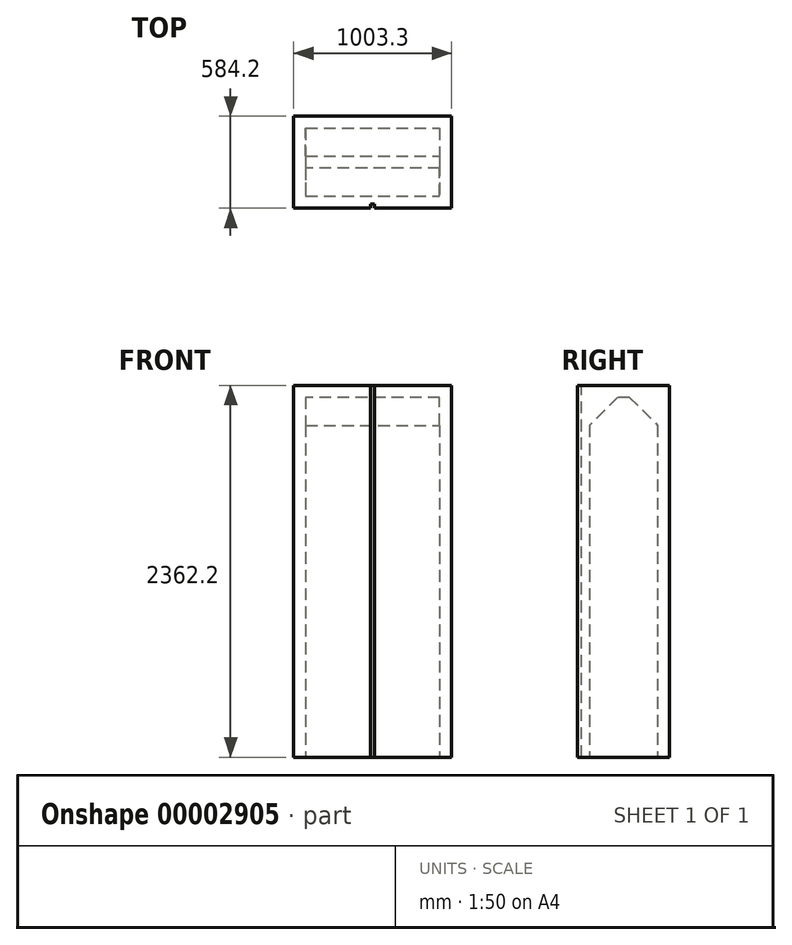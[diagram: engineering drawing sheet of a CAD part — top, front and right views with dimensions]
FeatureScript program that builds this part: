
annotation { "Feature Type Name" : "Feature", "Feature Type Description" : "" }
export const myFeature = defineFeature(function(context is Context, id is Id, definition is map)
    precondition{}
    {
        {
            var Q0;
            Q0=qCreatedBy(makeId("Top.planeOp"),FACE);
            var sketch = newSketch(context, id + "F0", { "sketchPlane" : qUnion([Q0])});
            skLineSegment(sketch, "E0.bottom", {"start": v(-500, 215.46) * mm, "end": v(503.3, 215.46) * mm});
            skLineSegment(sketch, "E0.top", {"start": v(-500, -368.74) * mm, "end": v(503.3, -368.74) * mm});
            skLineSegment(sketch, "E0.left", {"start": v(-500, 215.46) * mm, "end": v(-500, -368.74) * mm});
            skLineSegment(sketch, "E0.right", {"start": v(503.3, 215.46) * mm, "end": v(503.3, -368.74) * mm});
            skSolve(sketch);
        }
        {
            var Q0;
            Q0 = qSketchRegion(id + "F0", true);
            extrude(context, id + "F1", {"entities" : qUnion([Q0]), "depth" : 2362.2 * mm});
        }
        {
            var Q0;
            Q0=makeQuery(id+"F1.opExtrude","SWEPT_FACE",FACE,{"disambiguationData":[OSD([sQuery(id+"F0.wireOp",EDGE,"E0.top")])]});
            var sketch = newSketch(context, id + "F2", { "sketchPlane" : qUnion([Q0])});
            skLineSegment(sketch, "E1.bottom", {"start": v(12.7, 0) * mm, "end": v(-12.7, 0) * mm});
            skLineSegment(sketch, "E1.top", {"start": v(12.7, 2362.2) * mm, "end": v(-12.7, 2362.2) * mm});
            skLineSegment(sketch, "E1.left", {"start": v(12.7, 0) * mm, "end": v(12.7, 2362.2) * mm});
            skLineSegment(sketch, "E1.right", {"start": v(-12.7, 0) * mm, "end": v(-12.7, 2362.2) * mm});
            skSolve(sketch);
        }
        {
            var Q0;
            Q0 = qSketchRegion(id + "F2", true);
            extrude(context, id + "F3", {"entities" : qUnion([Q0]), "operationType" : NewBodyOperationType.REMOVE, "oppositeDirection" : true, "depth" : 25.4 * mm});
        }
        {
            var Q0;
            Q0=makeQuery(id+"F1.opExtrude","CAP_FACE",FACE,{"disambiguationData":[OSD([sQuery(id+"F0.wireOp",EDGE,"E0.bottom"),sQuery(id+"F0.wireOp",EDGE,"E0.top"),sQuery(id+"F0.wireOp",EDGE,"E0.left"),sQuery(id+"F0.wireOp",EDGE,"E0.right")])],"isStart":true});
            shell(context, id + "F4", {"entities" : qUnion([Q0]), "thickness" : 76.2 * mm});
        }
        {
            var Q0;
            Q0=makeQuery(id+"F1.opExtrude","CAP_FACE",FACE,{"disambiguationData":[OSD([sQuery(id+"F0.wireOp",EDGE,"E0.bottom"),sQuery(id+"F0.wireOp",EDGE,"E0.top"),sQuery(id+"F0.wireOp",EDGE,"E0.left"),sQuery(id+"F0.wireOp",EDGE,"E0.right")])],"isStart":true});
            var sketch = newSketch(context, id + "F5", { "sketchPlane" : qUnion([Q0])});
            skLineSegment(sketch, "E2.bottom", {"start": v(-88.9, 267.14) * mm, "end": v(88.9, 267.14) * mm});
            skLineSegment(sketch, "E2.top", {"start": v(-88.9, 292.54) * mm, "end": v(88.9, 292.54) * mm});
            skLineSegment(sketch, "E2.left", {"start": v(-88.9, 267.14) * mm, "end": v(-88.9, 292.54) * mm});
            skLineSegment(sketch, "E2.right", {"start": v(88.9, 267.14) * mm, "end": v(88.9, 292.54) * mm});
            skSolve(sketch);
        }
        {
            var Q0;
            Q0 = qSketchRegion(id + "F5", true);
            var Q1;
            Q1=makeQuery(id+"F4.opShell","OFFSET_FACE",FACE,{"disambiguationData":[OSD([sQuery(id+"F0.wireOp",EDGE,"E0.bottom"),sQuery(id+"F0.wireOp",EDGE,"E0.top"),sQuery(id+"F0.wireOp",EDGE,"E0.left"),sQuery(id+"F0.wireOp",EDGE,"E0.right")])]});
            extrude(context, id + "F6", {"entities" : qUnion([Q0]), "operationType" : NewBodyOperationType.REMOVE, "endBound" : BoundingType.UP_TO_SURFACE, "oppositeDirection" : true, "endBoundEntityFace" : qUnion([Q1]), "depth" : 25.4 * mm});
        }
        {
            var Q0;
            {var subQ0=sQuery(id+"F0.wireOp",EDGE,"E0.top");var subQ1=makeQuery(id+"F1.opExtrude","CAP_EDGE",EDGE,{"disambiguationData":[OSD([subQ0])],"isStart":false});var subQ2=sQuery(id+"F0.wireOp",EDGE,"E0.left");var subQ4=sQuery(id+"F0.wireOp",EDGE,"E0.right");Q0=makeQuery(id+"F6.boolean.opBoolean","MERGE",EDGE,{"derivedFrom":[makeQuery(id+"F4.opShell","OFFSET_EDGE",EDGE,{"disambiguationData":[OSD([subQ0]),TDD([makeQuery(id+"F3.boolean.opBoolean","SPLIT",EDGE,{"disambiguationData":[TD([makeQuery(id+"F1.opExtrude","SWEPT_FACE",FACE,{"disambiguationData":[OSD([subQ2])]})])],"derivedFrom":subQ1})])]}),makeQuery(id+"F4.opShell","OFFSET_EDGE",EDGE,{"disambiguationData":[OSD([subQ0]),TDD([makeQuery(id+"F3.boolean.opBoolean","SPLIT",EDGE,{"disambiguationData":[TD([makeQuery(id+"F1.opExtrude","SWEPT_FACE",FACE,{"disambiguationData":[OSD([subQ4])]})])],"derivedFrom":subQ1})])]}),makeQuery(id+"F6.opExtrude","CAP_EDGE",EDGE,{"disambiguationData":[OSD([sQuery(id+"F5.wireOp",EDGE,"E2.top")])],"isStart":false})]});}
            var Q1;
            {var subQ0=sQuery(id+"F0.wireOp",EDGE,"E0.bottom");Q1=makeQuery(id+"F4.opShell","OFFSET_EDGE",EDGE,{"disambiguationData":[OSD([subQ0]),TDD([makeQuery(id+"F1.opExtrude","CAP_EDGE",EDGE,{"disambiguationData":[OSD([subQ0])],"isStart":false})])]});}
            chamfer(context, id + "F7", {"entities" : qUnion([Q0, Q1]), "width" : 177.8 * mm, "tangentPropagation" : true});
        }
    });
